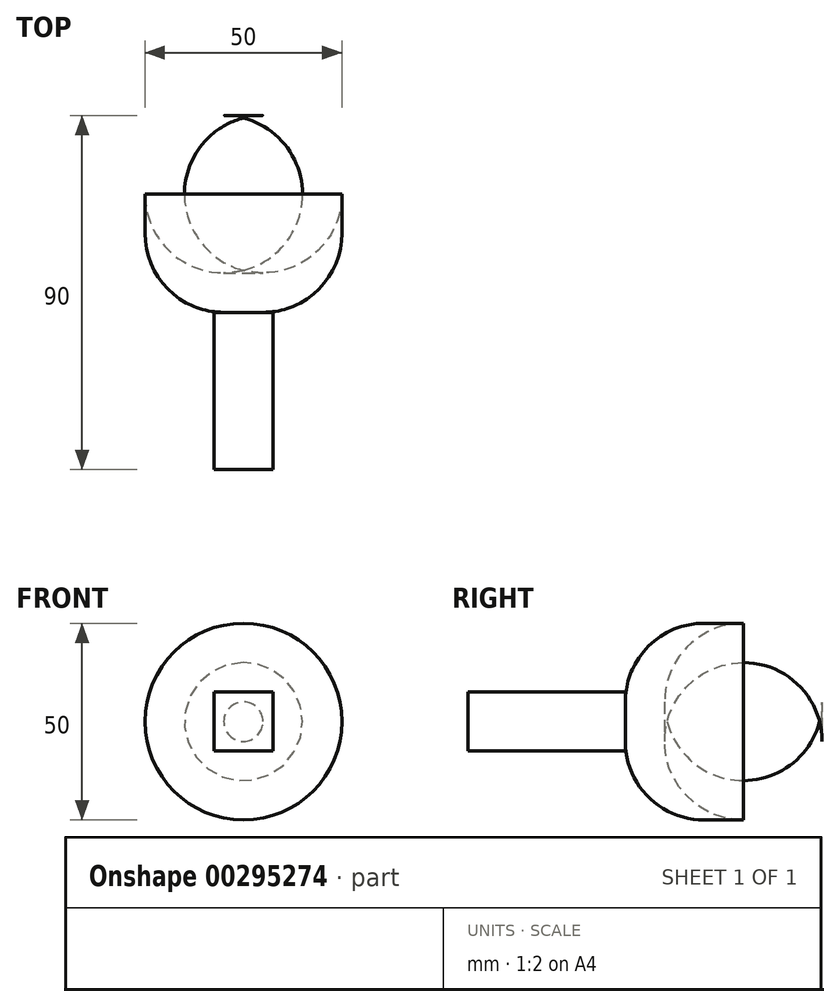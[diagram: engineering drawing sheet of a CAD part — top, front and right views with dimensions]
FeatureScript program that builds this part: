
annotation { "Feature Type Name" : "Feature", "Feature Type Description" : "" }
export const myFeature = defineFeature(function(context is Context, id is Id, definition is map)
    precondition{}
    {
        {
            var Q0;
            Q0=qCreatedBy(makeId("Front.planeOp"),FACE);
            var sketch = newSketch(context, id + "F0", { "sketchPlane" : qUnion([Q0])});
            skCircle(sketch, "E0", {"center": v(0, 0) * mm, "radius": 25 * mm});
            skSolve(sketch);
        }
        {
            var Q0;
            Q0=qSketchRegion(id+"F0",true);
            extrude(context, id + "F1", {"entities" : qUnion([Q0]), "depth" : 50 * mm});
        }
        {
            var Q0;
            Q0=makeQuery(id+"F1.opExtrude","CAP_FACE",FACE,{"disambiguationData":[OSD([sQuery(id+"F0.wireOp",EDGE,"E0")])],"isStart":false});
            var sketch = newSketch(context, id + "F2", { "sketchPlane" : qUnion([Q0])});
            skSolve(sketch);
        }
        {
            var Q0;
            Q0=makeQuery(id+"F1.opExtrude","CAP_EDGE",EDGE,{"disambiguationData":[OSD([sQuery(id+"F0.wireOp",EDGE,"E0")])],"isStart":false});
            fillet(context, id + "F3", {"entities" : qUnion([Q0]), "radius" : 20 * mm, "tangentPropagation" : true, "allowEdgeOverflow" : false});
        }
        {
            var Q0;
            Q0=makeQuery(id+"F1.opExtrude","CAP_EDGE",EDGE,{"disambiguationData":[OSD([sQuery(id+"F0.wireOp",EDGE,"E0")])],"isStart":true});
            fillet(context, id + "F4", {"entities" : qUnion([Q0]), "radius" : 20 * mm, "tangentPropagation" : true, "allowEdgeOverflow" : false});
        }
        {
            var Q0;
            Q0=makeQuery(id+"F2.imprint","IMPRINT",FACE,{"disambiguationData":[TD([[makeQuery(id+"F2.imprint","IMPRINT",EDGE,{"derivedFrom":makeQuery(id+"F1.opExtrude","CAP_EDGE",EDGE,{"disambiguationData":[OSD([sQuery(id+"F0.wireOp",EDGE,"E0")])],"isStart":false})}),1.0]])]});
            var sketch = newSketch(context, id + "F5", { "sketchPlane" : qUnion([Q0])});
            skLineSegment(sketch, "E1.bottom", {"start": v(-7.5, 7.5) * mm, "end": v(7.5, 7.5) * mm});
            skLineSegment(sketch, "E1.top", {"start": v(-7.5, -7.5) * mm, "end": v(7.5, -7.5) * mm});
            skLineSegment(sketch, "E1.left", {"start": v(-7.5, 7.5) * mm, "end": v(-7.5, -7.5) * mm});
            skLineSegment(sketch, "E1.right", {"start": v(7.5, 7.5) * mm, "end": v(7.5, -7.5) * mm});
            skSolve(sketch);
        }
        {
            var Q0;
            Q0=qSketchRegion(id+"F5",true);
            extrude(context, id + "F6", {"entities" : qUnion([Q0]), "operationType" : NewBodyOperationType.ADD, "depth" : 40 * mm});
        }
    });
